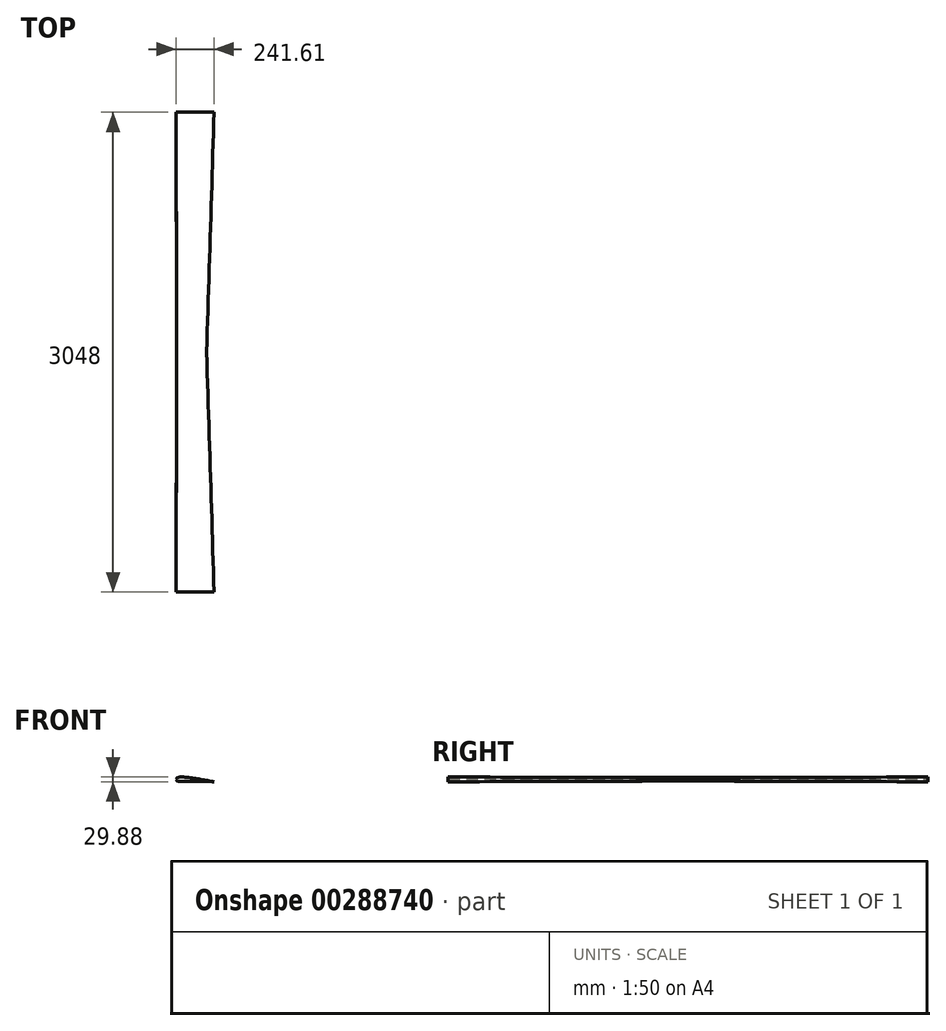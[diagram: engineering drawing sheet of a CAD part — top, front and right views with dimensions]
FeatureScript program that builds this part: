
annotation { "Feature Type Name" : "Feature", "Feature Type Description" : "" }
export const myFeature = defineFeature(function(context is Context, id is Id, definition is map)
    precondition{}
    {
        {
            var Q0;
            Q0=qCreatedBy(makeId("Front.planeOp"),FACE);
            var sketch = newSketch(context, id + "F0", { "sketchPlane" : qUnion([Q0])});
            skLineSegment(sketch, "E0", {"start": v(0, 0) * mm, "end": v(-190.24, 9.97) * mm, "construction": true});
            skFitSpline(sketch, "E1", {"points": [v(0, 0) * mm, v(-190.24, 9.97) * mm, v(-131.7, 70.56) * mm], "startDerivative": vector(-428.37, 16.1) * mm, "endDerivative": vector(151.17, 175.9) * mm});
            skFitSpline(sketch, "E2", {"points": [v(0, 0) * mm, v(-190.24, 9.97) * mm], "startDerivative": vector(-190.24, 9.97) * mm, "endDerivative": vector(-190.24, 9.97) * mm});
            skFitSpline(sketch, "E3", {"points": [v(0, 0) * mm, v(-167.75, 20.86) * mm, v(-190.24, 9.97) * mm, v(-145.3, -32.49) * mm], "startDerivative": vector(-392.53, 69.54) * mm, "endDerivative": vector(176.94, -181.91) * mm});
            skSolve(sketch);
        }
        {
            var Q0;
            Q0 = qSketchRegion(id + "F0", true);
            extrude(context, id + "F1", {"entities" : qUnion([Q0]), "endBound" : BoundingType.SYMMETRIC, "depth" : 3048 * mm, "hasDraft" : true, "draftAngle" : 0.12 * degree});
        }
    });
